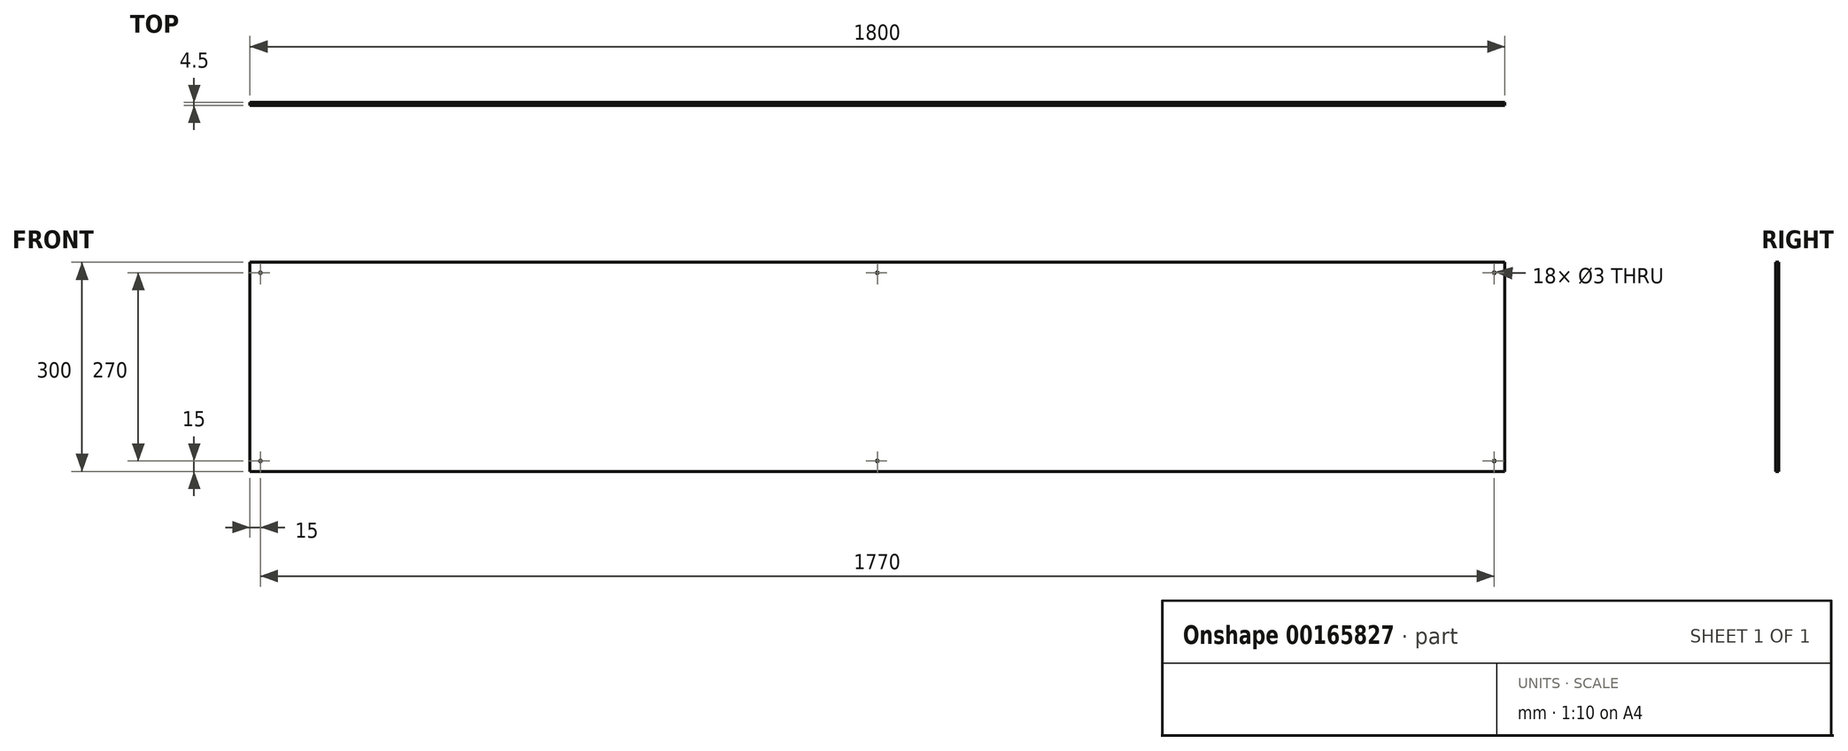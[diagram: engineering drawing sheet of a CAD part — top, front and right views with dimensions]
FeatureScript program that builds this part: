
annotation { "Feature Type Name" : "Feature", "Feature Type Description" : "" }
export const myFeature = defineFeature(function(context is Context, id is Id, definition is map)
    precondition{}
    {
        {
            var Q0;
            Q0=qCreatedBy(makeId("Front.planeOp"),FACE);
            var sketch = newSketch(context, id + "F0", { "sketchPlane" : qUnion([Q0])});
            skLineSegment(sketch, "E0.bottom", {"start": v(0, 0) * mm, "end": v(1800, 0) * mm});
            skLineSegment(sketch, "E0.top", {"start": v(0, 300) * mm, "end": v(1800, 300) * mm});
            skLineSegment(sketch, "E0.left", {"start": v(0, 0) * mm, "end": v(0, 300) * mm});
            skLineSegment(sketch, "E0.right", {"start": v(1800, 0) * mm, "end": v(1800, 300) * mm});
            skLineSegment(sketch, "E1", {"start": v(900, 300) * mm, "end": v(900, 0) * mm, "construction": true});
            skCircle(sketch, "E2", {"center": v(15, 285) * mm, "radius": 1.5 * mm});
            skCircle(sketch, "E3", {"center": v(900, 285) * mm, "radius": 1.5 * mm});
            skCircle(sketch, "E4", {"center": v(1785, 285) * mm, "radius": 1.5 * mm});
            skCircle(sketch, "E5", {"center": v(15, 15) * mm, "radius": 1.5 * mm});
            skCircle(sketch, "E6", {"center": v(900, 15) * mm, "radius": 1.5 * mm});
            skCircle(sketch, "E7", {"center": v(1785, 15) * mm, "radius": 1.5 * mm});
            skSolve(sketch);
        }
        {
            var Q0;
            Q0 = qSketchRegion(id + "F0", true);
            extrude(context, id + "F1", {"entities" : qUnion([Q0]), "depth" : 4.5 * mm});
        }
    });
